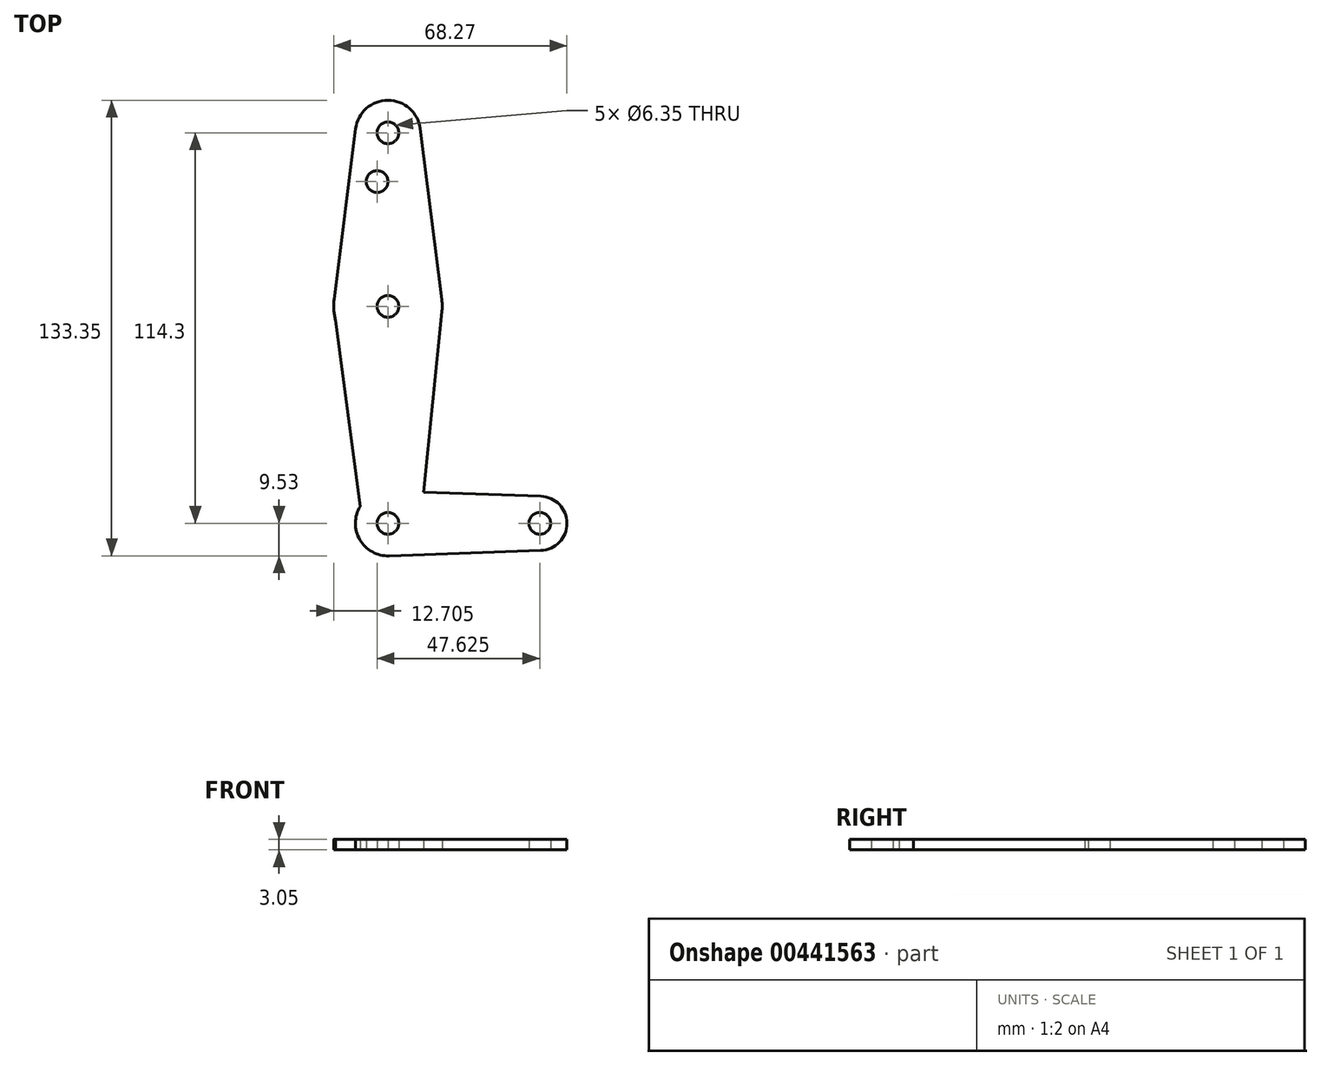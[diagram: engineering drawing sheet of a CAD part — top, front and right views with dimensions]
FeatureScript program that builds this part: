
annotation { "Feature Type Name" : "Feature", "Feature Type Description" : "" }
export const myFeature = defineFeature(function(context is Context, id is Id, definition is map)
    precondition{}
    {
        {
            var Q0;
            Q0=qCreatedBy(makeId("Top.planeOp"),FACE);
            var sketch = newSketch(context, id + "F0", { "sketchPlane" : qUnion([Q0])});
            skCircle(sketch, "E0", {"center": v(0, 0) * mm, "radius": 15.88 * mm});
            skCircle(sketch, "E1", {"center": v(0, 50.8) * mm, "radius": 9.53 * mm});
            skCircle(sketch, "E2", {"center": v(0, -63.5) * mm, "radius": 9.53 * mm});
            skCircle(sketch, "E3", {"center": v(44.45, -63.5) * mm, "radius": 7.94 * mm});
            skLineSegment(sketch, "E4", {"start": v(0, 50.8) * mm, "end": v(0, -63.5) * mm, "construction": true});
            skLineSegment(sketch, "E5", {"start": v(0, -63.5) * mm, "end": v(44.45, -63.5) * mm, "construction": true});
            skLineSegment(sketch, "E6", {"start": v(-9.45, 52) * mm, "end": v(-15.75, 1.98) * mm});
            skLineSegment(sketch, "E7", {"start": v(9.45, 52) * mm, "end": v(16, 0) * mm});
            skLineSegment(sketch, "E8", {"start": v(0.34, -73.02) * mm, "end": v(44.73, -71.43) * mm});
            skCircle(sketch, "E9", {"center": v(-3.17, 36.53) * mm, "radius": 3.18 * mm});
            skCircle(sketch, "E10", {"center": v(0, 50.8) * mm, "radius": 3.18 * mm});
            skCircle(sketch, "E11", {"center": v(0, 0) * mm, "radius": 3.18 * mm});
            skCircle(sketch, "E12", {"center": v(0, -63.5) * mm, "radius": 3.18 * mm});
            skCircle(sketch, "E13", {"center": v(44.45, -63.5) * mm, "radius": 3.18 * mm});
            skLineSegment(sketch, "E14", {"start": v(15.8, -1.59) * mm, "end": v(9.48, -64.45) * mm});
            skLineSegment(sketch, "E15", {"start": v(0.34, -53.98) * mm, "end": v(44.73, -55.57) * mm});
            skLineSegment(sketch, "E16", {"start": v(-15.88, 0) * mm, "end": v(-8.12, -58.53) * mm});
            skSolve(sketch);
        }
        {
            var Q0;
            Q0 = qSketchRegion(id + "F0", true);
            extrude(context, id + "F1", {"entities" : qUnion([Q0]), "depth" : 3.05 * mm});
        }
    });
